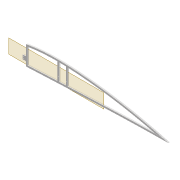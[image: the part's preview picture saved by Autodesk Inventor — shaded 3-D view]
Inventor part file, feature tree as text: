
AUTODESK INVENTOR PART (.ipt)
format: ipt  version: 2022 (Build 260153000, 153)  size: 415,744 bytes
history: native  units: mm
features: extrude x8, sketch x7, projected_geometry x6, fillet x2, shell x1, plane x1
ambient origin geometry x8: Origin, YZ Plane, XZ Plane, XY Plane, X Axis, Y Axis, Z Axis, Center Point
bodies: Solid1 (feature_tree)
feature tree (25):
  extrude  "Extrusion1"  Depth=5.0mm
  shell  "Shell1"  Thickness=2.0mm
  extrude  "Extrusion8"  Depth=5.9mm
  extrude  "Extrusion3"  Depth=10.0mm TaperAngle=0.0deg
  extrude  "Extrusion4"  Depth=2.0mm
  fillet  "Fillet1"  Radius=5.0mm
  sketch  "Sketch10"  dims[d22=4.0mm d23=0.0mm d31=2.0mm d32=5.0mm]
  extrude  "Extrusion5"  Depth=2.5mm
  plane  "Work Plane2"
  extrude  "Extrusion9"  Depth=1.6mm
  fillet  "Fillet2"  Radius=2.5mm
  extrude  "Extrusion10"  Depth=0.5mm
  extrude  "Extrusion11"  Depth=0.5mm TaperAngle=0.0deg
  sketch  "Sketch3"  dims[d0=4.0mm d1=0.0mm d2=5.0mm d7=2.0mm]
  sketch  "Sketch8"  dims[d8=2.0mm d9=5.9mm]
  sketch  "Sketch9"  dims[d13=10.0mm d14=0.0mm d16=10.0mm d17=0.0mm]
  projected_geometry  "Projected Loop4"
  projected_geometry  "Projected Loop10"
  sketch  "Sketch24"  dims[d34=1.6mm d35=2.5mm]
  projected_geometry  "Projected Loop11"
  projected_geometry  "Projected Loop12"
  projected_geometry  "Projected Loop13"
  sketch  "Sketch26"  dims[d37=5.0mm d38=1.6mm d40=2.5mm]
  projected_geometry  "Projected Loop14"
  sketch  "Sketch27"  dims[d62=80.0mm d63=6.0mm d64=4.0mm d65=0.0mm d66=3.0mm d67=12.0mm d68=5.0mm d69=10.0mm d70=12.0mm d71=3.05mm d72=10.0mm d73=0.0mm d74=2.0mm d75=100.0mm d76=20.0mm d77=0.5mm d78=10.0mm d79=0.0mm d80=10.0mm d81=0.0mm]
